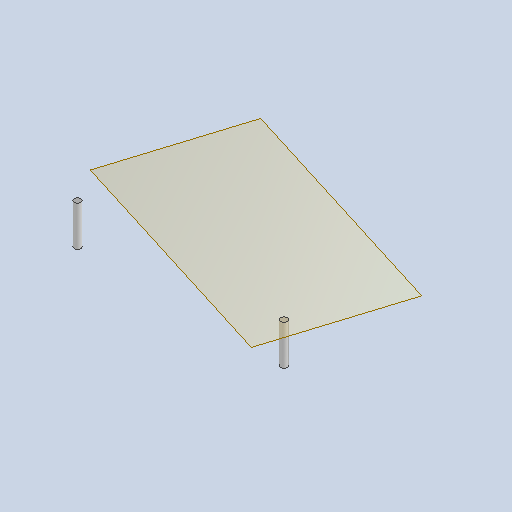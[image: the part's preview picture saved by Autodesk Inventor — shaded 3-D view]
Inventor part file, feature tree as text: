
AUTODESK INVENTOR PART (.ipt)
format: ipt  version: 2025.1 (Build 291241000, 241)  size: 140,288 bytes
history: native  units: mm
features: extrude x2, sketch x2, reference x2, other x2, plane x1
ambient origin geometry x8: Origin, YZ Plane, XZ Plane, XY Plane, X Axis, Y Axis, Z Axis, Center Point
bodies: Solid1 (feature_tree)
feature tree (9):
  extrude  "Extrusion1"  Depth=24.0mm TaperAngle=0.0deg
  plane  "Work Plane1"
  extrude  "Extrusion2"  [1 undecoded]
  sketch  "Sketch1"  dims[d0=24.0mm d1=0.0mm d2=24.0mm d3=0.0mm]
  reference  "Reference1"
  sketch  "Sketch2"
  reference  "Reference2"
  other  "<userpath>\Documents\Inventor\Single cylinder Steam Engine\asembly.iam"
  other  "asembly.iam"
note: 1 required parameter value undecoded (feature->parameter linkage not recoverable at this tier; creation-order binding heuristic only, values carry confidence <= 0.55)
